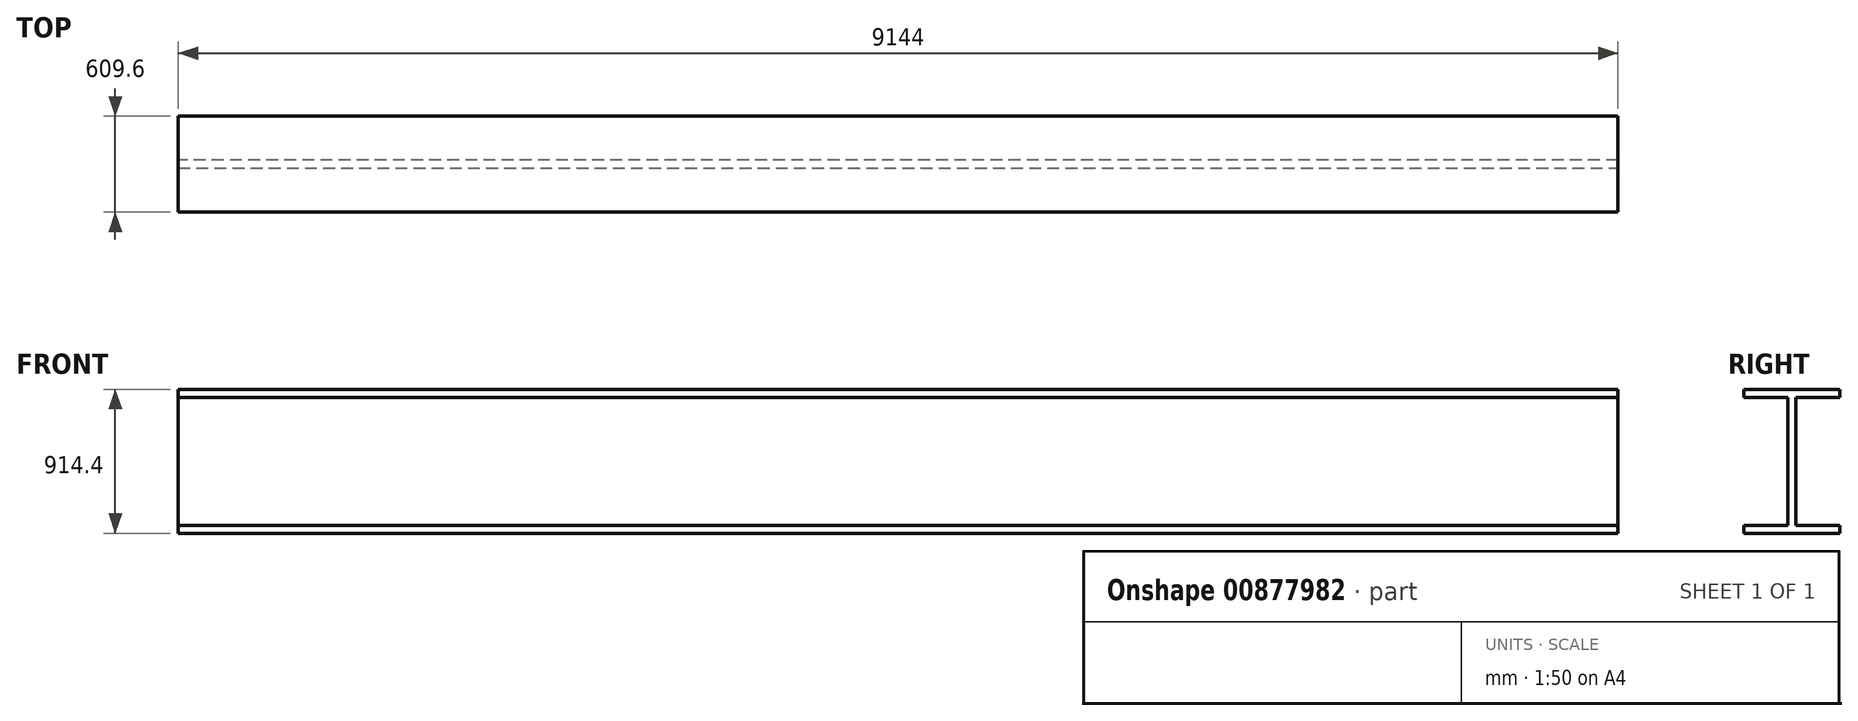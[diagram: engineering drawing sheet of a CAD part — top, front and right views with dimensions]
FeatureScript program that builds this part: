
annotation { "Feature Type Name" : "Feature", "Feature Type Description" : "" }
export const myFeature = defineFeature(function(context is Context, id is Id, definition is map)
    precondition{}
    {
        {
            var Q0;
            Q0=qCreatedBy(makeId("Top.planeOp"),FACE);
            var sketch = newSketch(context, id + "F0", { "sketchPlane" : qUnion([Q0])});
            skLineSegment(sketch, "E0.bottom", {"start": v(-4574.15, -345.04) * mm, "end": v(4569.85, -345.04) * mm});
            skLineSegment(sketch, "E0.top", {"start": v(-4574.15, -954.64) * mm, "end": v(4569.85, -954.64) * mm});
            skLineSegment(sketch, "E0.left", {"start": v(-4574.15, -345.04) * mm, "end": v(-4574.15, -954.64) * mm});
            skLineSegment(sketch, "E0.right", {"start": v(4569.85, -345.04) * mm, "end": v(4569.85, -954.64) * mm});
            skSolve(sketch);
        }
        {
            var Q0;
            Q0 = qSketchRegion(id + "F0", true);
            extrude(context, id + "F1", {"entities" : qUnion([Q0]), "depth" : 914.4 * mm, "offsetDistance" : 25.4 * mm});
        }
        {
            var Q0;
            Q0=makeQuery(id+"F1.opExtrude","SWEPT_FACE",FACE,{"disambiguationData":[OSD([sQuery(id+"F0.wireOp",EDGE,"E0.top")])]});
            var sketch = newSketch(context, id + "F2", { "sketchPlane" : qUnion([Q0])});
            skLineSegment(sketch, "E1.bottom", {"start": v(-4574.15, 863.6) * mm, "end": v(4569.85, 863.6) * mm});
            skLineSegment(sketch, "E1.top", {"start": v(-4574.15, 50.8) * mm, "end": v(4569.85, 50.8) * mm});
            skLineSegment(sketch, "E1.left", {"start": v(-4574.15, 863.6) * mm, "end": v(-4574.15, 50.8) * mm});
            skLineSegment(sketch, "E1.right", {"start": v(4569.85, 863.6) * mm, "end": v(4569.85, 50.8) * mm});
            skSolve(sketch);
        }
        {
            var Q0;
            Q0=makeQuery(id+"F2.imprint","IMPRINT",FACE,{"disambiguationData":[TD([[makeQuery(id+"F2.imprint","IMPRINT",EDGE,{"derivedFrom":sQuery(id+"F2.wireOp",EDGE,"E1.bottom")}),-1.0]])]});
            extrude(context, id + "F3", {"entities" : qUnion([Q0]), "operationType" : NewBodyOperationType.REMOVE, "oppositeDirection" : true, "depth" : 279.4 * mm, "offsetDistance" : 25.4 * mm});
        }
        {
            var Q0;
            Q0=makeQuery(id+"F1.opExtrude","SWEPT_FACE",FACE,{"disambiguationData":[OSD([sQuery(id+"F0.wireOp",EDGE,"E0.bottom")])]});
            var sketch = newSketch(context, id + "F4", { "sketchPlane" : qUnion([Q0])});
            skLineSegment(sketch, "E2.bottom", {"start": v(-4569.85, 863.6) * mm, "end": v(4574.15, 863.6) * mm});
            skLineSegment(sketch, "E2.top", {"start": v(-4569.85, 50.8) * mm, "end": v(4574.15, 50.8) * mm});
            skLineSegment(sketch, "E2.left", {"start": v(-4569.85, 863.6) * mm, "end": v(-4569.85, 50.8) * mm});
            skLineSegment(sketch, "E2.right", {"start": v(4574.15, 863.6) * mm, "end": v(4574.15, 50.8) * mm});
            skSolve(sketch);
        }
        {
            var Q0;
            Q0 = qSketchRegion(id + "F4", true);
            extrude(context, id + "F5", {"entities" : qUnion([Q0]), "operationType" : NewBodyOperationType.REMOVE, "oppositeDirection" : true, "depth" : 279.4 * mm, "offsetDistance" : 25.4 * mm});
        }
    });
